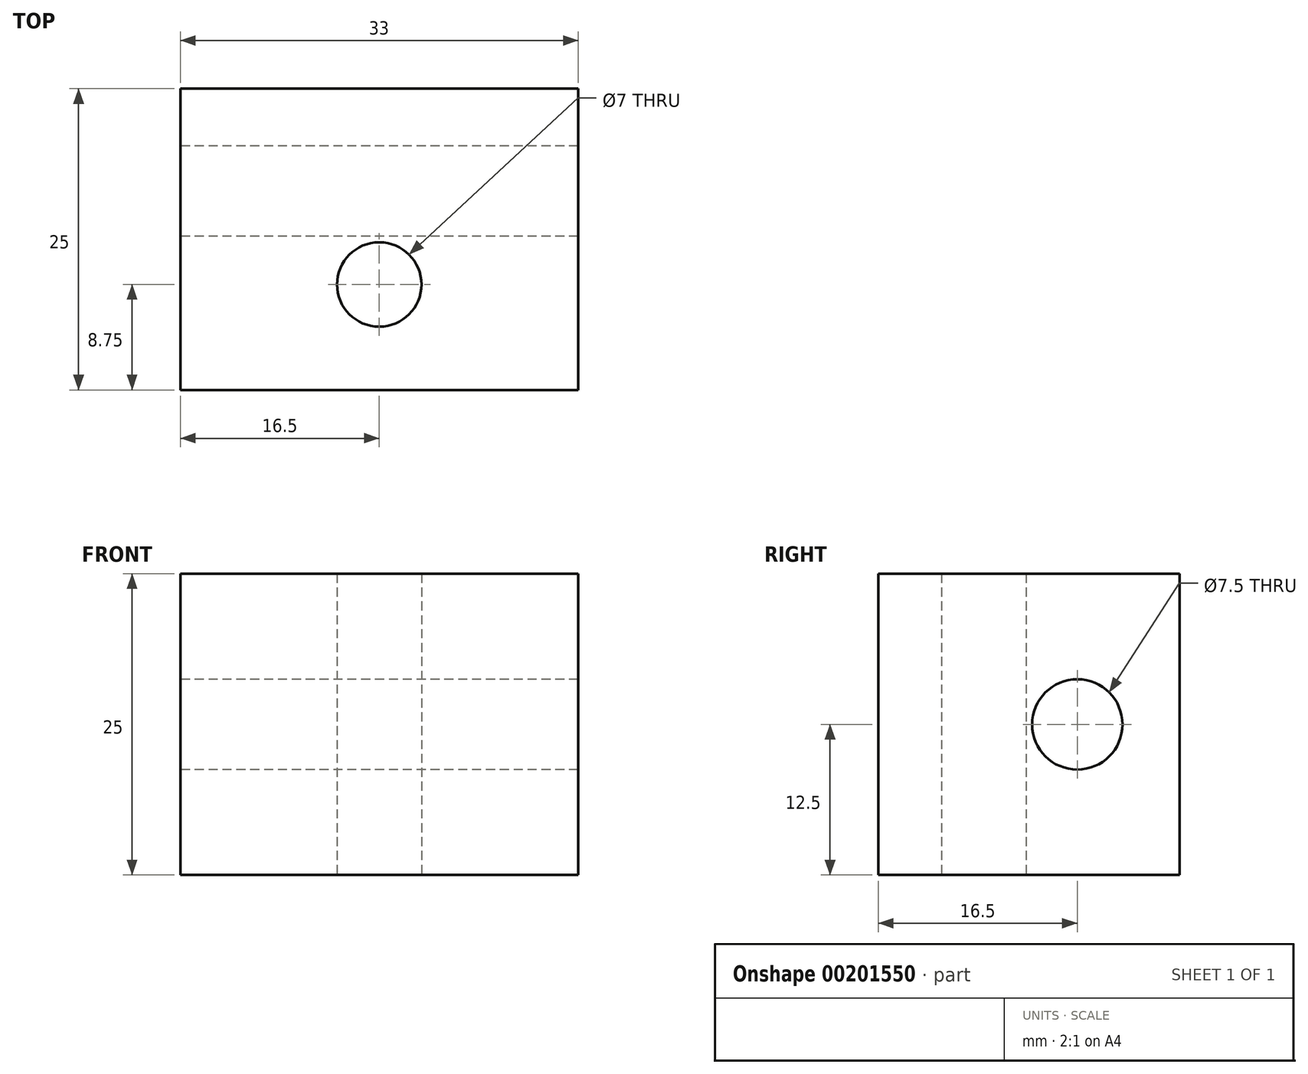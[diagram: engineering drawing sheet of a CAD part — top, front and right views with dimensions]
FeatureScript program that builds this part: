
annotation { "Feature Type Name" : "Feature", "Feature Type Description" : "" }
export const myFeature = defineFeature(function(context is Context, id is Id, definition is map)
    precondition{}
    {
        {
            var Q0;
            Q0=qCreatedBy(makeId("Front.planeOp"),FACE);
            var sketch = newSketch(context, id + "F0", { "sketchPlane" : qUnion([Q0])});
            skLineSegment(sketch, "E0.bottom", {"start": v(0, 0) * mm, "end": v(33, 0) * mm});
            skLineSegment(sketch, "E0.top", {"start": v(0, 25) * mm, "end": v(33, 25) * mm});
            skLineSegment(sketch, "E0.left", {"start": v(0, 0) * mm, "end": v(0, 25) * mm});
            skLineSegment(sketch, "E0.right", {"start": v(33, 0) * mm, "end": v(33, 25) * mm});
            skSolve(sketch);
        }
        {
            var Q0;
            Q0 = qSketchRegion(id + "F0", true);
            extrude(context, id + "F1", {"entities" : qUnion([Q0]), "depth" : 25 * mm});
        }
        {
            var Q0;
            Q0=qCreatedBy(makeId("Top.planeOp"),FACE);
            var sketch = newSketch(context, id + "F2", { "sketchPlane" : qUnion([Q0])});
            skLineSegment(sketch, "E1", {"start": v(16.5, 10.85) * mm, "end": v(16.5, -33.87) * mm, "construction": true});
            skLineSegment(sketch, "E2", {"start": v(-10.7, -16.25) * mm, "end": v(47.18, -16.25) * mm, "construction": true});
            skCircle(sketch, "E3", {"center": v(16.5, -16.25) * mm, "radius": 3.5 * mm});
            skLineSegment(sketch, "E4", {"start": v(-10.6, -12.5) * mm, "end": v(55.83, -12.5) * mm, "construction": true});
            skSolve(sketch);
        }
        {
            var Q0;
            Q0 = qSketchRegion(id + "F2", true);
            extrude(context, id + "F3", {"entities" : qUnion([Q0]), "operationType" : NewBodyOperationType.REMOVE, "endBound" : BoundingType.THROUGH_ALL, "depth" : 25 * mm});
        }
        {
            var Q0;
            Q0=qCreatedBy(makeId("Right.planeOp"),FACE);
            var sketch = newSketch(context, id + "F4", { "sketchPlane" : qUnion([Q0])});
            skLineSegment(sketch, "E5", {"start": v(-12.5, 32.07) * mm, "end": v(-12.5, -12.87) * mm, "construction": true});
            skLineSegment(sketch, "E6", {"start": v(-8.5, 33.45) * mm, "end": v(-8.5, -12.87) * mm, "construction": true});
            skLineSegment(sketch, "E7", {"start": v(9.56, 12.5) * mm, "end": v(-33.6, 12.5) * mm, "construction": true});
            skCircle(sketch, "E8", {"center": v(-8.5, 12.5) * mm, "radius": 3.75 * mm});
            skSolve(sketch);
        }
        {
            var Q0;
            Q0=makeQuery(id+"F4.imprint","IMPRINT",FACE,{"disambiguationData":[TD([[makeQuery(id+"F4.imprint","IMPRINT",EDGE,{"derivedFrom":sQuery(id+"F4.wireOp",EDGE,"E8")}),1.0]])]});
            var Q1;
            Q1=sQuery(id+"F4.wireOp",EDGE,"E8");
            extrude(context, id + "F5", {"entities" : qUnion([Q0]), "operationType" : NewBodyOperationType.REMOVE, "surfaceEntities" : qUnion([Q1]), "endBound" : BoundingType.THROUGH_ALL, "depth" : 25 * mm});
        }
    });
